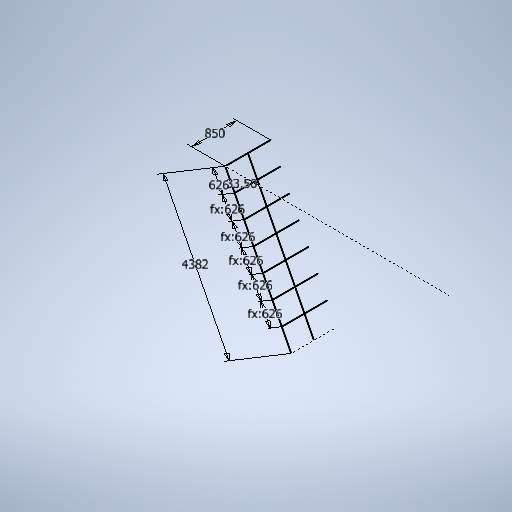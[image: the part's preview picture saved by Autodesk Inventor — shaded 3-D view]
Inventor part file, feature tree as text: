
AUTODESK INVENTOR PART (.ipt)
format: ipt  version: 2025.1 (Build 291241020, 241B)  size: 268,288 bytes
history: native  units: in
note: dims shown in document units (in); Inventor stores cm internally (conversion verified against a paired STEP export)
features: sketch x1
ambient origin geometry x8: Origin, YZ Plane, XZ Plane, XY Plane, X Axis, Y Axis, Z Axis, Center Point
feature tree (1):
  sketch  "Sketch3"  dims[d7=172.5197in d8=33.4646in d9=0.2302in d10=24.6457in d11=24.6457in d12=24.6457in d13=24.6457in d14=24.6457in d15=24.6457in]
